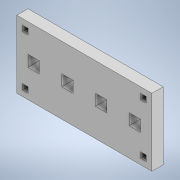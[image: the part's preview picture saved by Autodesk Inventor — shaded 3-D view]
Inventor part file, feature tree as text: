
AUTODESK INVENTOR PART (.ipt)
format: ipt  version: 2020.2 (Build 242310000, 310)  size: 185,344 bytes
history: native  units: mm
features: extrude x2, sketch x2
ambient origin geometry x8: Origin, YZ Plane, XZ Plane, XY Plane, X Axis, Y Axis, Z Axis, Center Point
bodies: Body1 (feature_tree)
feature tree (4):
  extrude  "Extrusion4"  Depth=120.0mm
  extrude  "Extrusion5"  Depth=60.0mm
  sketch  "Esquisse8"
  sketch  "Esquisse9"
